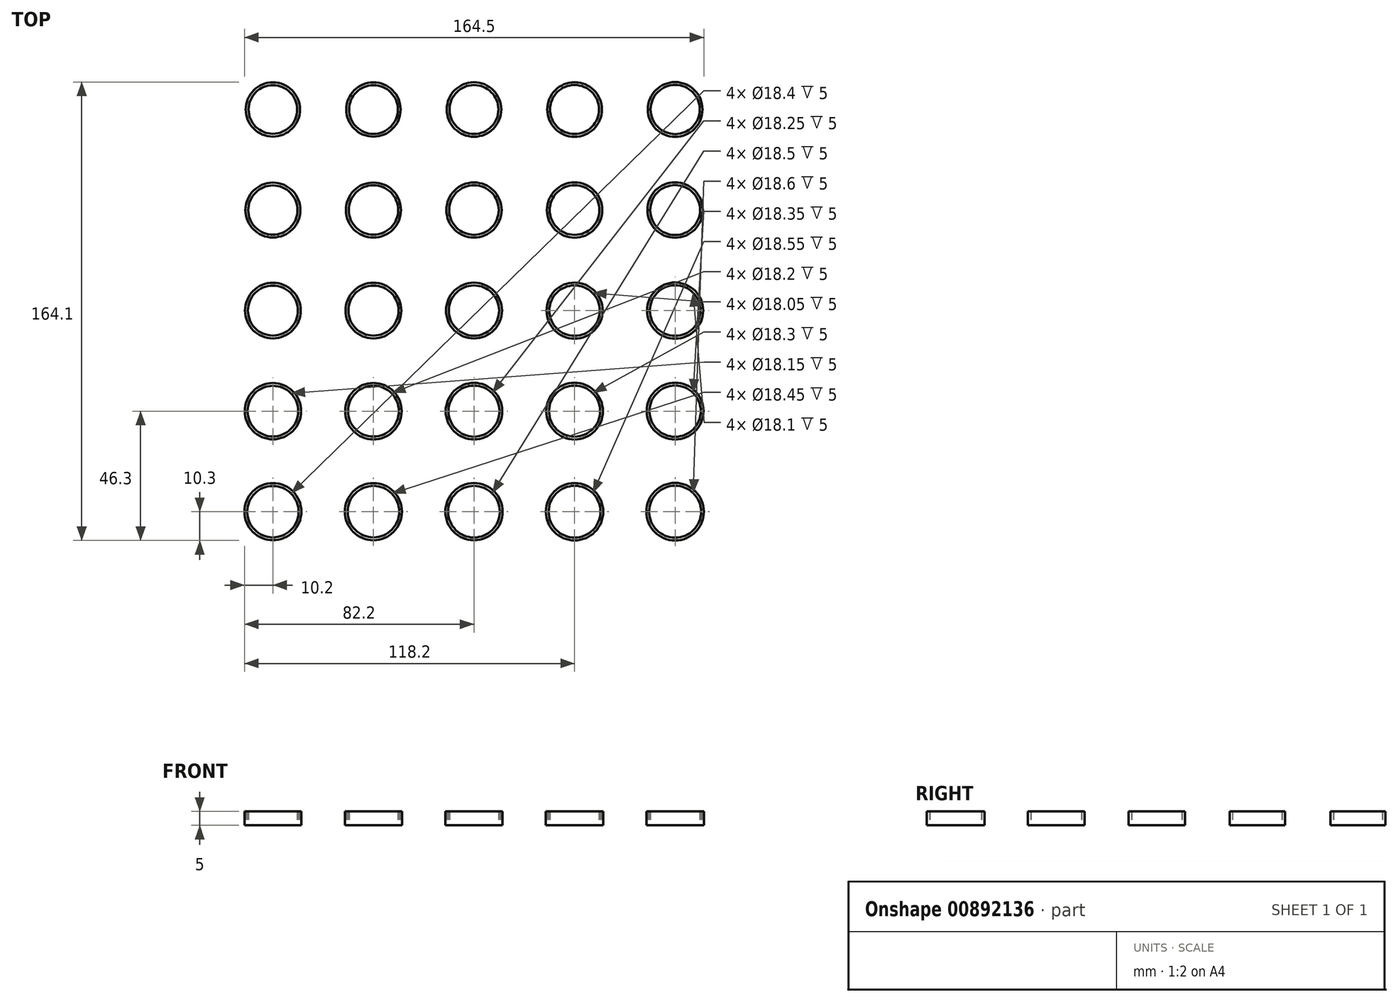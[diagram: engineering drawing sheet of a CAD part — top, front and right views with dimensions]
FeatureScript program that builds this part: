
annotation { "Feature Type Name" : "Feature", "Feature Type Description" : "" }
export const myFeature = defineFeature(function(context is Context, id is Id, definition is map)
    precondition{}
    {
        {
            var Q0;
            Q0=qCreatedBy(makeId("Top.planeOp"),FACE);
            var sketch = newSketch(context, id + "F0", { "sketchPlane" : qUnion([Q0])});
            skLineSegment(sketch, "E0.bottom", {"start": v(90, 90) * mm, "end": v(-90, 90) * mm, "construction": true});
            skLineSegment(sketch, "E0.top", {"start": v(90, -90) * mm, "end": v(-90, -90) * mm, "construction": true});
            skLineSegment(sketch, "E0.left", {"start": v(90, 90) * mm, "end": v(90, -90) * mm, "construction": true});
            skLineSegment(sketch, "E0.right", {"start": v(-90, 90) * mm, "end": v(-90, -90) * mm, "construction": true});
            skPoint(sketch, "E0.middle", {"position": v(0, 0) * mm});
            skCircle(sketch, "E1", {"center": v(0, 0) * mm, "radius": 9 * mm});
            skLineSegment(sketch, "E2", {"start": v(-90, 0) * mm, "end": v(90, 0) * mm, "construction": true});
            skLineSegment(sketch, "E3", {"start": v(0, 90) * mm, "end": v(0, -90) * mm, "construction": true});
            skCircle(sketch, "E4.0.1.0", {"center": v(0, 36) * mm, "radius": 8.88 * mm});
            skLineSegment(sketch, "E4.0.1.1", {"start": v(-90, 36) * mm, "end": v(90, 36) * mm, "construction": true});
            skCircle(sketch, "E4.0.2.0", {"center": v(0, 72) * mm, "radius": 8.75 * mm});
            skCircle(sketch, "E4.1.0.0", {"center": v(36, 0) * mm, "radius": 9.03 * mm});
            skCircle(sketch, "E4.1.1.0", {"center": v(36, 36) * mm, "radius": 8.9 * mm});
            skCircle(sketch, "E4.1.2.0", {"center": v(36, 72) * mm, "radius": 8.78 * mm});
            skCircle(sketch, "E4.2.0.0", {"center": v(72, 0) * mm, "radius": 9.05 * mm});
            skCircle(sketch, "E4.2.1.0", {"center": v(72, 36) * mm, "radius": 8.93 * mm});
            skCircle(sketch, "E4.2.2.0", {"center": v(72, 72) * mm, "radius": 8.8 * mm});
            skLineSegment(sketch, "E4.direction1", {"start": v(0, 0) * mm, "end": v(36, 0) * mm, "construction": true});
            skLineSegment(sketch, "E4.direction2", {"start": v(0, 0) * mm, "end": v(0, 36) * mm, "construction": true});
            skCircle(sketch, "E5.MirrorC", {"center": v(-36, 72) * mm, "radius": 8.72 * mm});
            skCircle(sketch, "E6.MirrorC", {"center": v(-36, 36) * mm, "radius": 8.85 * mm});
            skCircle(sketch, "E7.MirrorC", {"center": v(-72, 36) * mm, "radius": 8.82 * mm});
            skCircle(sketch, "E8.MirrorC", {"center": v(-72, 72) * mm, "radius": 8.7 * mm});
            skCircle(sketch, "E9.MirrorC", {"center": v(-36, 0) * mm, "radius": 8.97 * mm});
            skCircle(sketch, "E10.MirrorC", {"center": v(-72, 0) * mm, "radius": 8.95 * mm});
            skCircle(sketch, "E11.MirrorC", {"center": v(0, -36) * mm, "radius": 9.12 * mm});
            skCircle(sketch, "E12.MirrorC", {"center": v(-72, -72) * mm, "radius": 9.2 * mm});
            skCircle(sketch, "E13.MirrorC", {"center": v(-72, -36) * mm, "radius": 9.07 * mm});
            skCircle(sketch, "E14.MirrorC", {"center": v(-36, -72) * mm, "radius": 9.23 * mm});
            skCircle(sketch, "E15.MirrorC", {"center": v(-36, -36) * mm, "radius": 9.1 * mm});
            skCircle(sketch, "E16.MirrorC", {"center": v(36, -36) * mm, "radius": 9.15 * mm});
            skCircle(sketch, "E17.MirrorC", {"center": v(36, -72) * mm, "radius": 9.28 * mm});
            skCircle(sketch, "E18.MirrorC", {"center": v(72, -36) * mm, "radius": 9.18 * mm});
            skCircle(sketch, "E19.MirrorC", {"center": v(72, -72) * mm, "radius": 9.3 * mm});
            skCircle(sketch, "E20.MirrorC", {"center": v(0, -72) * mm, "radius": 9.25 * mm});
            skCircle(sketch, "E21.0", {"center": v(-72, 72) * mm, "radius": 9.7 * mm});
            skCircle(sketch, "E22.0", {"center": v(-36, 72) * mm, "radius": 9.73 * mm});
            skCircle(sketch, "E23.0", {"center": v(0, 72) * mm, "radius": 9.75 * mm});
            skCircle(sketch, "E24.0", {"center": v(36, 72) * mm, "radius": 9.77 * mm});
            skCircle(sketch, "E25.0", {"center": v(72, 72) * mm, "radius": 9.8 * mm});
            skCircle(sketch, "E26.0", {"center": v(-72, 36) * mm, "radius": 9.83 * mm});
            skCircle(sketch, "E27.0", {"center": v(-36, 36) * mm, "radius": 9.85 * mm});
            skCircle(sketch, "E28.0", {"center": v(0, 36) * mm, "radius": 9.88 * mm});
            skCircle(sketch, "E29.0", {"center": v(36, 36) * mm, "radius": 9.9 * mm});
            skCircle(sketch, "E30.0", {"center": v(72, 36) * mm, "radius": 9.92 * mm});
            skCircle(sketch, "E31.0", {"center": v(-72, 0) * mm, "radius": 9.95 * mm});
            skCircle(sketch, "E32.0", {"center": v(-36, 0) * mm, "radius": 9.98 * mm});
            skCircle(sketch, "E33.0", {"center": v(0, 0) * mm, "radius": 10 * mm});
            skCircle(sketch, "E34.0", {"center": v(36, 0) * mm, "radius": 10.02 * mm});
            skCircle(sketch, "E35.0", {"center": v(72, 0) * mm, "radius": 10.05 * mm});
            skCircle(sketch, "E36.0", {"center": v(-72, -36) * mm, "radius": 10.08 * mm});
            skCircle(sketch, "E37.0", {"center": v(-36, -36) * mm, "radius": 10.1 * mm});
            skCircle(sketch, "E38.0", {"center": v(0, -36) * mm, "radius": 10.12 * mm});
            skCircle(sketch, "E39.0", {"center": v(36, -36) * mm, "radius": 10.15 * mm});
            skCircle(sketch, "E40.0", {"center": v(72, -36) * mm, "radius": 10.18 * mm});
            skCircle(sketch, "E41.0", {"center": v(-72, -72) * mm, "radius": 10.2 * mm});
            skCircle(sketch, "E42.0", {"center": v(-36, -72) * mm, "radius": 10.23 * mm});
            skCircle(sketch, "E43.0", {"center": v(0, -72) * mm, "radius": 10.25 * mm});
            skCircle(sketch, "E44.0", {"center": v(36, -72) * mm, "radius": 10.27 * mm});
            skCircle(sketch, "E45.0", {"center": v(72, -72) * mm, "radius": 10.3 * mm});
            skSolve(sketch);
        }
        {
            var Q0;
            Q0 = qSketchRegion(id + "F0", true);
            extrude(context, id + "F1", {"entities" : qUnion([Q0]), "depth" : 5 * mm, "offsetDistance" : 25 * mm});
        }
    });
